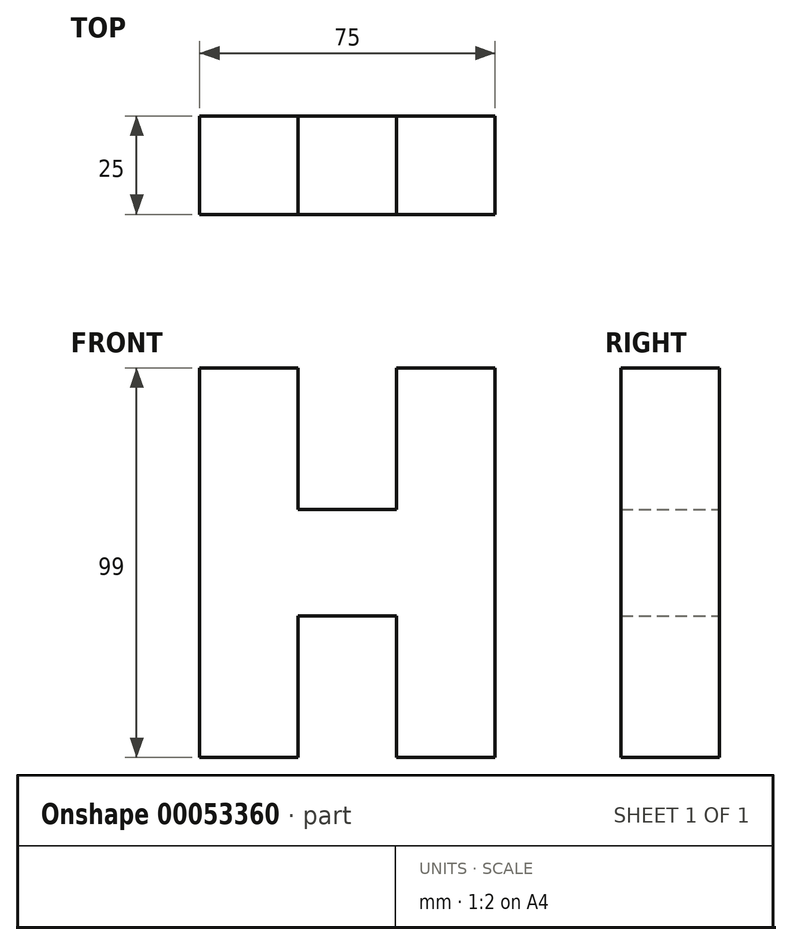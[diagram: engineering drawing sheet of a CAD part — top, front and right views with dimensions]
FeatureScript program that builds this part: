
annotation { "Feature Type Name" : "Feature", "Feature Type Description" : "" }
export const myFeature = defineFeature(function(context is Context, id is Id, definition is map)
    precondition{}
    {
        {
            var Q0;
            Q0=qCreatedBy(makeId("Front.planeOp"),FACE);
            var sketch = newSketch(context, id + "F0", { "sketchPlane" : qUnion([Q0])});
            skLineSegment(sketch, "E0.rect.bottom", {"start": v(37.5, -49.5) * mm, "end": v(12.5, -49.5) * mm});
            skLineSegment(sketch, "E0.rect.top", {"start": v(37.5, 49.5) * mm, "end": v(12.5, 49.5) * mm});
            skLineSegment(sketch, "E0.rect.left", {"start": v(37.5, -49.5) * mm, "end": v(37.5, 49.5) * mm});
            skLineSegment(sketch, "E0.rect.right", {"start": v(-37.5, -49.5) * mm, "end": v(-37.5, 49.5) * mm});
            skPoint(sketch, "E0.rect.middle", {"position": v(0, 0) * mm});
            skLineSegment(sketch, "E1.trimOffspring", {"start": v(-12.5, 49.5) * mm, "end": v(-37.5, 49.5) * mm});
            skLineSegment(sketch, "E2.trimOffspring", {"start": v(-12.5, -49.5) * mm, "end": v(-37.5, -49.5) * mm});
            skLineSegment(sketch, "E3", {"start": v(-12.5, 13.5) * mm, "end": v(12.5, 13.5) * mm});
            skLineSegment(sketch, "E4", {"start": v(-12.5, -13.5) * mm, "end": v(12.5, -13.5) * mm});
            skLineSegment(sketch, "E5", {"start": v(-12.5, 49.5) * mm, "end": v(-12.5, 13.5) * mm});
            skLineSegment(sketch, "E6", {"start": v(12.5, 13.5) * mm, "end": v(12.5, 49.5) * mm});
            skLineSegment(sketch, "E7", {"start": v(12.5, -13.5) * mm, "end": v(12.5, -49.5) * mm});
            skLineSegment(sketch, "E8", {"start": v(-12.5, -13.5) * mm, "end": v(-12.5, -49.5) * mm});
            skSolve(sketch);
        }
        {
            var Q0;
            Q0 = qSketchRegion(id + "F0", true);
            extrude(context, id + "F1", {"entities" : qUnion([Q0]), "depth" : 25 * mm});
        }
    });
